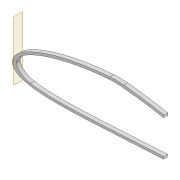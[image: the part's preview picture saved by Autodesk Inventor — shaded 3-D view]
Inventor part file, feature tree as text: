
AUTODESK INVENTOR PART (.ipt)
format: ipt  version: 2022 (Build 260153000, 153)  size: 551,424 bytes
history: native  units: mm
features: sketch x7, extrude x6, thicken_offset x4, projected_geometry x4, fillet x3, shell x1, plane x1, other x1
ambient origin geometry x8: Origin, YZ Plane, XZ Plane, XY Plane, X Axis, Y Axis, Z Axis, Center Point
bodies: Solid1 (feature_tree)
feature tree (27):
  extrude  "Extrusion1"  Depth=3.0mm
  shell  "Shell1"  Thickness=1.0mm
  thicken_offset  "Thicken1"
  extrude  "Extrusion27"  TaperAngle=0.0deg  [1 undecoded]
  thicken_offset  "Thicken3"
  extrude  "Extrusion29"  Depth=20.0mm
  plane  "Work Plane5"
  other  "Bend Part2"
  thicken_offset  "Thicken5"
  extrude  "Extrusion30"  Depth=5.0mm TaperAngle=0.0deg
  fillet  "Fillet6"  Radius=10.0mm
  extrude  "Extrusion31"  Depth=1.0mm
  fillet  "Fillet7"  Radius=50.0mm
  extrude  "Extrusion32"  Depth=5.0mm TaperAngle=0.0deg
  fillet  "Fillet8"  Radius=500.0mm
  thicken_offset  "Thicken6"
  sketch  "Sketch3"  dims[d0=5.0mm d1=0.0mm d2=3.0mm d159=1.0mm d160=2.0mm]
  sketch  "Sketch48"  dims[d236=190.0mm d237=0.0mm d238=0.0mm]
  sketch  "Sketch55"  dims[d249=2.0mm d250=1.0mm d254=20.0mm]
  projected_geometry  "Projected Loop32"
  sketch  "Sketch57"  dims[d255=8.0mm d256=5.0mm d257=0.0mm d262=10.0mm d263=0.174533mm]
  sketch  "Sketch58"  dims[d264=1.0mm d265=1.0mm d268=50.0mm]
  projected_geometry  "Projected Loop34"
  sketch  "Sketch59"  dims[d269=9.0mm d270=5.0mm d271=0.0mm d272=500.0mm]
  projected_geometry  "Projected Loop35"
  sketch  "Sketch60"  dims[d273=200.0mm d274=60.0mm d275=600.0mm d276=5.0mm d277=0.0mm d278=100.0mm d279=5.0mm d280=60.0mm d281=500.0mm d282=10.0mm d283=0.0mm d284=100.0mm d285=2.0mm d286=3.0mm]
  projected_geometry  "Projected Loop36"
note: 1 required parameter value undecoded (feature->parameter linkage not recoverable at this tier; creation-order binding heuristic only, values carry confidence <= 0.55)
